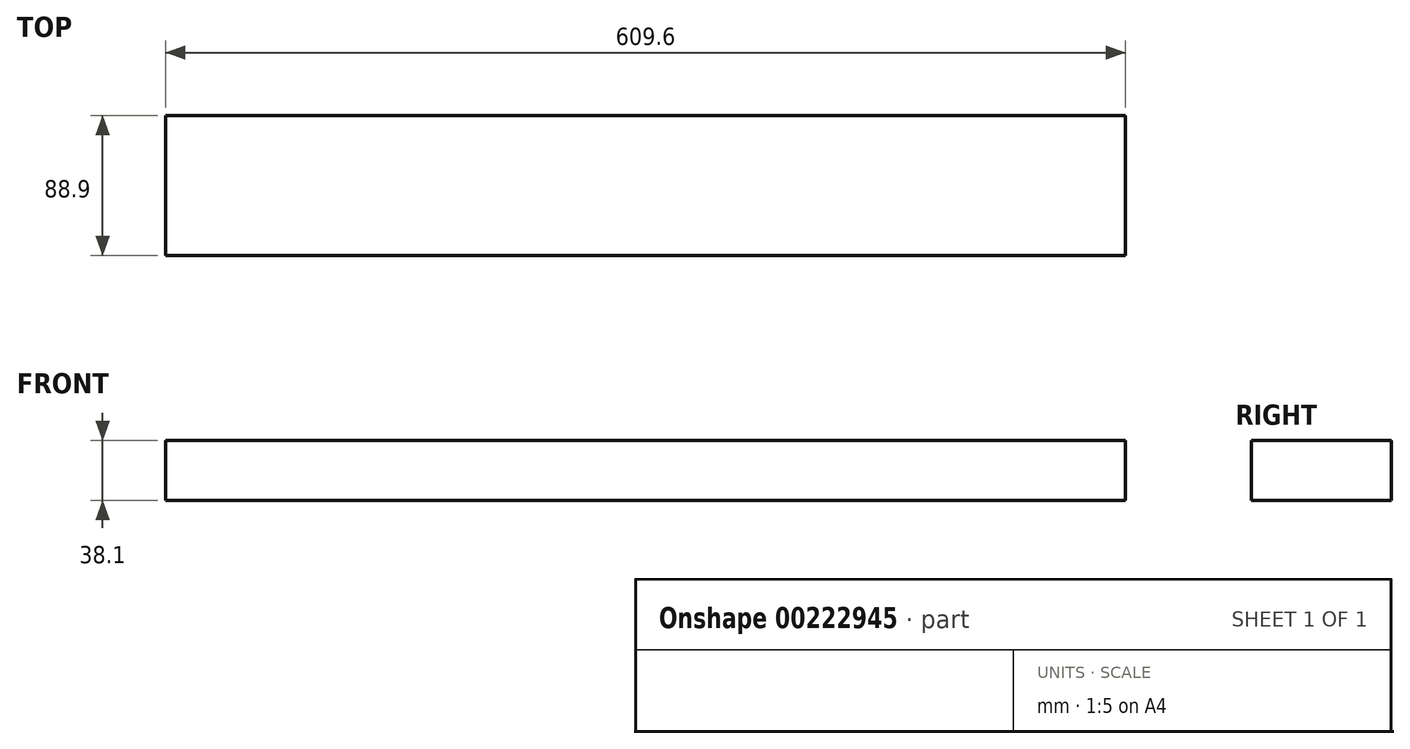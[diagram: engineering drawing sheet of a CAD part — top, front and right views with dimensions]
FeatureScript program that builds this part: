
annotation { "Feature Type Name" : "Feature", "Feature Type Description" : "" }
export const myFeature = defineFeature(function(context is Context, id is Id, definition is map)
    precondition{}
    {
        {
            var Q0;
            Q0=qCreatedBy(makeId("Top.planeOp"),FACE);
            var sketch = newSketch(context, id + "F0", { "sketchPlane" : qUnion([Q0])});
            skLineSegment(sketch, "E0.bottom", {"start": v(0, 0) * mm, "end": v(609.6, 0) * mm});
            skLineSegment(sketch, "E0.top", {"start": v(0, 88.9) * mm, "end": v(609.6, 88.9) * mm});
            skLineSegment(sketch, "E0.left", {"start": v(0, 0) * mm, "end": v(0, 88.9) * mm});
            skLineSegment(sketch, "E0.right", {"start": v(609.6, 0) * mm, "end": v(609.6, 88.9) * mm});
            skSolve(sketch);
        }
        {
            var Q0;
            Q0 = qSketchRegion(id + "F0", true);
            extrude(context, id + "F1", {"entities" : qUnion([Q0]), "depth" : 38.1 * mm});
        }
    });
